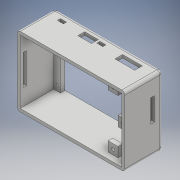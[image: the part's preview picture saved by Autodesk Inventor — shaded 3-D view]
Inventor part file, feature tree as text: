
AUTODESK INVENTOR PART (.ipt)
format: ipt  version: 2017 (Build 210142000, 142)  size: 392,704 bytes
history: native  units: mm
features: projected_geometry x11, sketch x9, extrude x9, hole x3, fillet x1
ambient origin geometry x8: Origin, YZ Plane, XZ Plane, XY Plane, X Axis, Y Axis, Z Axis, Center Point
bodies: Solid1 (feature_tree)
feature tree (33):
  sketch  "Sketch1"  dims[d0=67.0mm d1=42.0mm]
  extrude  "Extrusion1"  Depth=42.0mm
  hole  "Hole1"  [1 undecoded]
  extrude  "Extrusion2"  Depth=3.5mm
  fillet  "Fillet1"  Radius=2.5mm
  hole  "Hole2"  [1 undecoded]
  sketch  "Sketch4"  dims[d10=3.5mm d11=3.5mm]
  extrude  "Extrusion5"  Depth=6.5mm
  extrude  "Extrusion6"  Depth=4.5mm
  extrude  "Extrusion7"  Depth=3.0mm TaperAngle=0.0deg
  extrude  "Extrusion8"  Depth=15.0mm TaperAngle=0.0deg
  extrude  "Extrusion9"  Depth=7.5mm
  extrude  "Extrusion10"  Depth=7.5mm
  extrude  "Extrusion12"  Depth=5.0mm
  hole  "Hole5"  [1 undecoded]
  sketch  "Sketch2"  dims[d5=2.5mm d6=36.0mm]
  sketch  "Sketch3"  dims[d7=2.5mm d8=3.5mm d9=2.5mm]
  projected_geometry  "Projected Loop1"
  sketch  "Sketch6"  dims[d12=4.5mm d13=6.5mm]
  projected_geometry  "Projected Loop3"
  projected_geometry  "Projected Loop4"
  sketch  "Sketch7"  dims[d14=2.0mm d20=4.5mm]
  projected_geometry  "Projected Loop5"
  projected_geometry  "Projected Loop6"
  projected_geometry  "Projected Loop7"
  sketch  "Sketch10"  dims[d21=6.5mm d28=3.0mm d29=0.0mm]
  projected_geometry  "Projected Loop8"
  sketch  "Sketch11"  dims[d30=1.5mm d31=6.0mm d32=4.0mm d33=2.0mm d34=90.0deg d35=2.0mm d36=20.594885mm d37=15.0mm d38=0.0mm]
  projected_geometry  "Projected Loop9"
  projected_geometry  "Projected Loop10"
  projected_geometry  "Projected Loop11"
  sketch  "Sketch13"  dims[d39=2.0mm d40=7.5mm d41=7.5mm d42=5.5mm d43=6.0mm d44=4.0mm d45=2.0mm d46=90.0deg d47=5.0mm d48=20.594885mm d49=5.0mm d50=5.0mm d51=5.0mm d52=5.0mm d53=5.0mm d54=5.0mm d55=5.0mm d56=5.0mm d68=15.0mm d69=2.5mm d70=10.0mm d71=2.5mm d72=10.0mm d73=0.0mm d74=2.5mm d75=8.0mm d76=4.0mm d77=2.0mm d78=21.5mm d79=30.5mm d80=4.5mm d81=1.0mm d82=34.0mm d83=2.5mm d84=47.0mm d85=60.0mm d86=5.0mm d87=1.5mm d88=4.0mm d89=2.0mm d90=4.0mm d91=2.0mm d92=10.0mm d93=0.0mm d97=6.5mm d99=6.5mm d102=10.0mm d103=0.0mm d107=6.5mm d108=1.0mm d111=6.75mm d112=5.75mm d113=4.5mm d115=6.5mm d117=6.5mm d118=3.0mm d119=0.0mm d127=10.0mm d128=10.0mm d129=2.0mm d130=0.0mm d131=2.0mm d132=0.0mm d147=4.0mm d148=6.5mm d149=4.0mm d150=6.5mm d151=4.0mm d152=6.5mm d153=1.0mm d154=1.0mm d155=0.5mm d156=0.0mm d157=6.5mm d159=6.5mm d162=6.5mm d163=6.5mm d164=6.5mm d165=2.0mm d166=6.0mm d167=4.0mm d168=2.0mm d169=90.0deg d170=8.0mm d171=20.594885mm]
  projected_geometry  "Projected Loop13"
note: 3 required parameter values undecoded (feature->parameter linkage not recoverable at this tier; creation-order binding heuristic only, values carry confidence <= 0.55)
